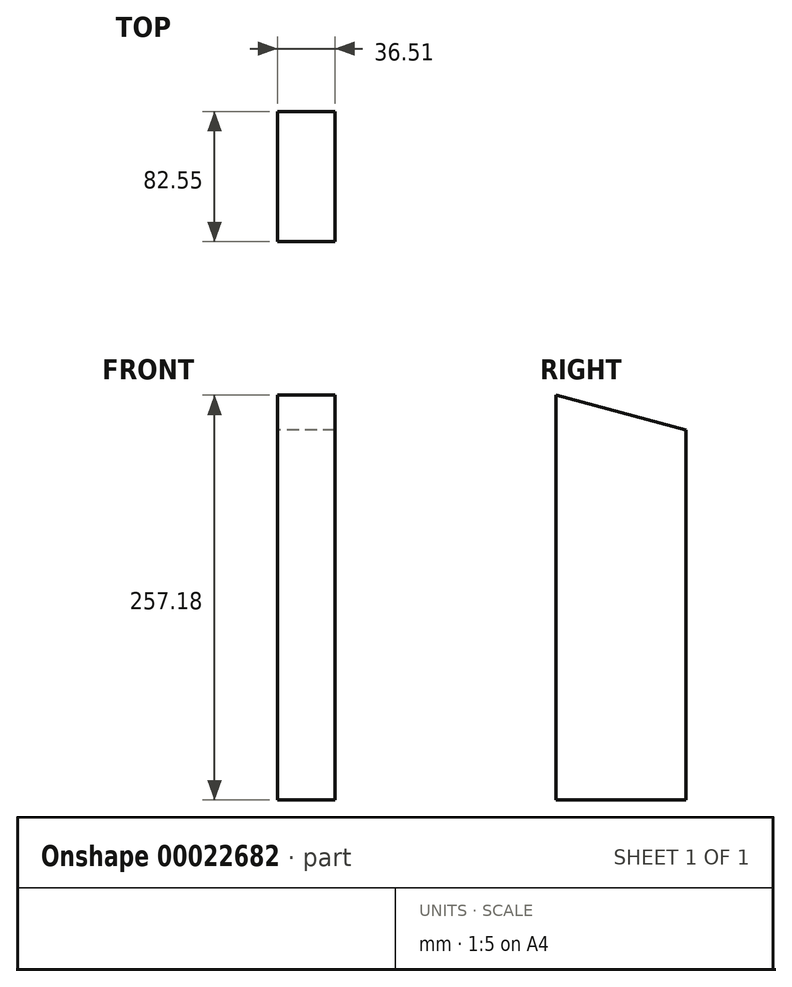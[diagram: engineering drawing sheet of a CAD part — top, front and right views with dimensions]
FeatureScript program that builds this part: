
annotation { "Feature Type Name" : "Feature", "Feature Type Description" : "" }
export const myFeature = defineFeature(function(context is Context, id is Id, definition is map)
    precondition{}
    {
        {
            var Q0;
            Q0=qCreatedBy(makeId("Right.planeOp"),FACE);
            var sketch = newSketch(context, id + "F0", { "sketchPlane" : qUnion([Q0])});
            skLineSegment(sketch, "E0", {"start": v(0, 0) * mm, "end": v(82.55, 0) * mm});
            skLineSegment(sketch, "E1", {"start": v(82.55, 0) * mm, "end": v(82.55, 234.95) * mm});
            skLineSegment(sketch, "E2", {"start": v(0, 0) * mm, "end": v(0, 257.18) * mm});
            skLineSegment(sketch, "E3", {"start": v(82.55, 234.95) * mm, "end": v(0, 257.18) * mm});
            skSolve(sketch);
        }
        {
            var Q0;
            Q0=qSketchRegion(id+"F0",true);
            extrude(context, id + "F1", {"entities" : qUnion([Q0]), "depth" : 36.5 * mm});
        }
    });
